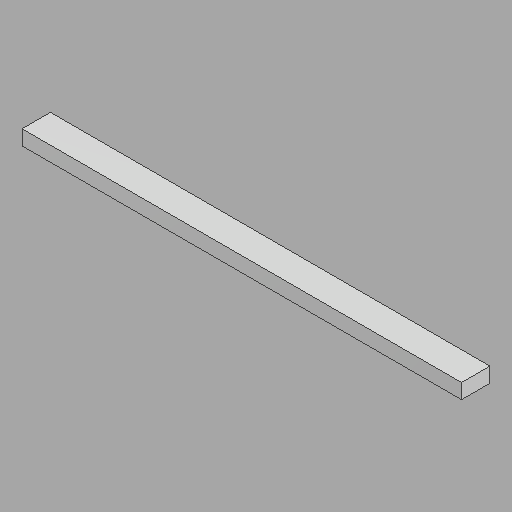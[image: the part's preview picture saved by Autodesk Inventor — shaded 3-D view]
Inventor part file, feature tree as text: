
AUTODESK INVENTOR PART (.ipt)
format: ipt  version: 2022.2 (Build 262287010, 287A)  size: 112,128 bytes
history: native  units: in
note: dims shown in document units (in); Inventor stores cm internally (conversion verified against a paired STEP export)
features: direct_edit x1, other x1, revolve x1
ambient origin geometry x8: Origin, YZ Plane, XZ Plane, XY Plane, X Axis, Y Axis, Z Axis, Center Point
bodies: Solid1 (feature_tree)
feature tree (3):
  direct_edit  "Direct Edit1"
  other  "Head (1) (1)"
  revolve  "Rotate1"  Angle=90.0deg
